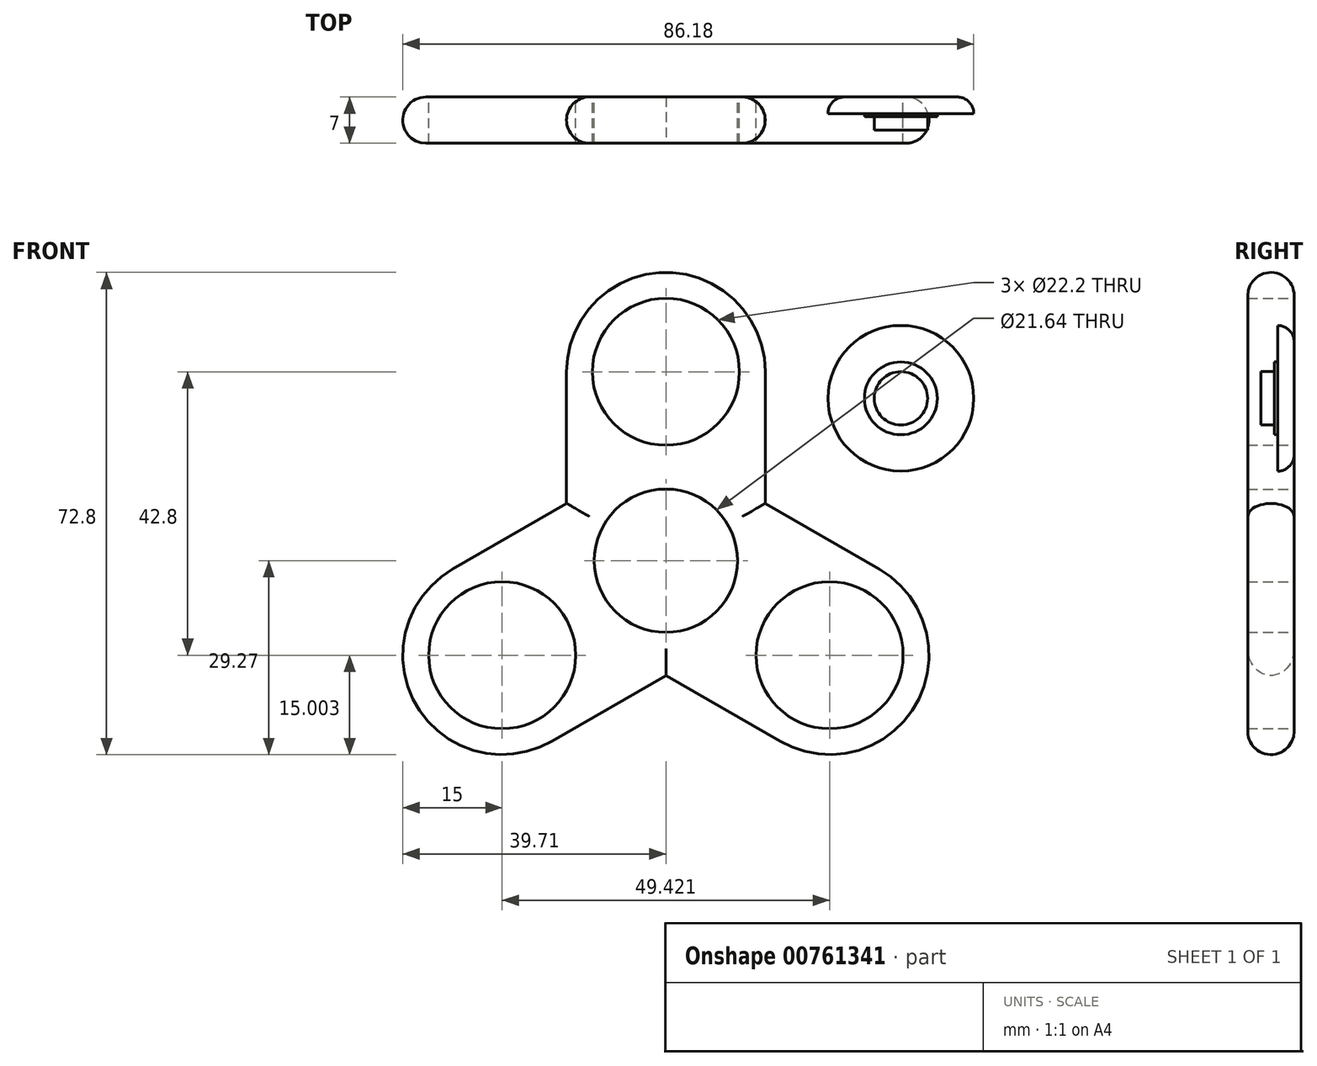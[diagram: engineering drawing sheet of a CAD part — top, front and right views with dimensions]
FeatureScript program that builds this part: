
annotation { "Feature Type Name" : "Feature", "Feature Type Description" : "" }
export const myFeature = defineFeature(function(context is Context, id is Id, definition is map)
    precondition{}
    {
        {
            var Q0;
            Q0=qCreatedBy(makeId("Front.planeOp"),FACE);
            var sketch = newSketch(context, id + "F0", { "sketchPlane" : qUnion([Q0])});
            skCircle(sketch, "E0", {"center": v(35.47, 24.52) * mm, "radius": 11 * mm});
            skCircle(sketch, "E1", {"center": v(35.47, 24.52) * mm, "radius": 5.5 * mm});
            skCircle(sketch, "E2", {"center": v(35.47, 24.52) * mm, "radius": 4.03 * mm});
            skSolve(sketch);
        }
        {
            var Q0;
            Q0=makeQuery(id+"F0.imprint","IMPRINT",FACE,{"disambiguationData":[TD([[makeQuery(id+"F0.imprint","IMPRINT",EDGE,{"derivedFrom":sQuery(id+"F0.wireOp",EDGE,"E0")}),1.0]])]});
            extrude(context, id + "F1", {"entities" : qUnion([Q0]), "depth" : 2.5 * mm, "offsetDistance" : 25 * mm});
        }
        {
            var Q0;
            Q0=makeQuery(id+"F0.imprint","IMPRINT",FACE,{"disambiguationData":[TD([[makeQuery(id+"F0.imprint","IMPRINT",EDGE,{"derivedFrom":sQuery(id+"F0.wireOp",EDGE,"E1")}),1.0]])]});
            extrude(context, id + "F2", {"entities" : qUnion([Q0]), "operationType" : NewBodyOperationType.ADD, "depth" : 3 * mm, "offsetDistance" : 25 * mm});
        }
        {
            var Q0;
            Q0=makeQuery(id+"F0.imprint","IMPRINT",FACE,{"disambiguationData":[TD([[makeQuery(id+"F0.imprint","IMPRINT",EDGE,{"derivedFrom":sQuery(id+"F0.wireOp",EDGE,"E2")}),1.0]])]});
            extrude(context, id + "F3", {"entities" : qUnion([Q0]), "operationType" : NewBodyOperationType.ADD, "depth" : 5 * mm, "offsetDistance" : 25 * mm});
        }
        {
            var Q0;
            Q0=makeQuery(id+"F1.opExtrude","CAP_EDGE",EDGE,{"disambiguationData":[OSD([sQuery(id+"F0.wireOp",EDGE,"E0")])],"isStart":true});
            fillet(context, id + "F4", {"entities" : qUnion([Q0]), "radius" : 2.5 * mm, "tangentPropagation" : true, "allowEdgeOverflow" : false});
        }
        {
            var Q0;
            Q0=qCreatedBy(makeId("Front.planeOp"),FACE);
            var sketch = newSketch(context, id + "F5", { "sketchPlane" : qUnion([Q0])});
            skCircle(sketch, "E3", {"center": v(0, 0) * mm, "radius": 10.82 * mm});
            skCircle(sketch, "E4", {"center": v(0, 28.53) * mm, "radius": 11.1 * mm});
            skCircle(sketch, "E5.1.0", {"center": v(-24.71, -14.27) * mm, "radius": 11.1 * mm});
            skCircle(sketch, "E5.2.0", {"center": v(24.71, -14.27) * mm, "radius": 11.1 * mm});
            skArc(sketch, "E6", {"start": v(15, 28.53) * mm, "mid": v(0, 43.53) * mm, "end": v(-15, 28.53) * mm});
            skLineSegment(sketch, "E7", {"start": v(-15, 28.53) * mm, "end": v(-15, 8.66) * mm});
            skLineSegment(sketch, "E8", {"start": v(15, 28.53) * mm, "end": v(15, 8.66) * mm});
            skLineSegment(sketch, "E9.1.0", {"start": v(-17.21, -27.26) * mm, "end": v(0, -17.32) * mm});
            skArc(sketch, "E9.1.1", {"start": v(-32.21, -1.28) * mm, "mid": v(-37.7, -21.77) * mm, "end": v(-17.21, -27.26) * mm});
            skLineSegment(sketch, "E9.1.2", {"start": v(-32.21, -1.28) * mm, "end": v(-15, 8.66) * mm});
            skLineSegment(sketch, "E9.2.0", {"start": v(32.21, -1.28) * mm, "end": v(15, 8.66) * mm});
            skArc(sketch, "E9.2.1", {"start": v(17.21, -27.26) * mm, "mid": v(37.7, -21.77) * mm, "end": v(32.21, -1.28) * mm});
            skLineSegment(sketch, "E9.2.2", {"start": v(17.21, -27.26) * mm, "end": v(0, -17.32) * mm});
            skPoint(sketch, "E10.orphan", {"position": v(-15, 6.28) * mm});
            skPoint(sketch, "E11.orphan", {"position": v(-13.67, 9.43) * mm});
            skPoint(sketch, "E12.orphan", {"position": v(12.94, 9.85) * mm});
            skPoint(sketch, "E13.orphan", {"position": v(15, 7.13) * mm});
            skPoint(sketch, "E14.orphan", {"position": v(2.06, -16.13) * mm});
            skPoint(sketch, "E15.orphan", {"position": v(-1.33, -16.55) * mm});
            skSolve(sketch);
        }
        {
            var Q0;
            Q0=makeQuery(id+"F5.imprint","IMPRINT",FACE,{"disambiguationData":[TD([[makeQuery(id+"F5.imprint","IMPRINT",EDGE,{"derivedFrom":sQuery(id+"F5.wireOp",EDGE,"E3")}),-1.0]])]});
            extrude(context, id + "F6", {"entities" : qUnion([Q0]), "depth" : 7 * mm, "offsetDistance" : 25 * mm});
        }
        {
            var Q0;
            Q0=makeQuery(id+"F6.opExtrude","CAP_EDGE",EDGE,{"disambiguationData":[OSD([sQuery(id+"F5.wireOp",EDGE,"E9.1.2")])],"isStart":false});
            var Q1;
            Q1=makeQuery(id+"F6.opExtrude","CAP_EDGE",EDGE,{"disambiguationData":[OSD([sQuery(id+"F5.wireOp",EDGE,"E9.1.1")])],"isStart":false});
            var Q2;
            Q2=makeQuery(id+"F6.opExtrude","CAP_EDGE",EDGE,{"disambiguationData":[OSD([sQuery(id+"F5.wireOp",EDGE,"E9.1.0")])],"isStart":false});
            var Q3;
            Q3=makeQuery(id+"F6.opExtrude","CAP_EDGE",EDGE,{"disambiguationData":[OSD([sQuery(id+"F5.wireOp",EDGE,"E9.2.2")])],"isStart":false});
            var Q4;
            Q4=makeQuery(id+"F6.opExtrude","CAP_EDGE",EDGE,{"disambiguationData":[OSD([sQuery(id+"F5.wireOp",EDGE,"E9.2.1")])],"isStart":false});
            var Q5;
            Q5=makeQuery(id+"F6.opExtrude","CAP_EDGE",EDGE,{"disambiguationData":[OSD([sQuery(id+"F5.wireOp",EDGE,"E8")])],"isStart":false});
            var Q6;
            Q6=makeQuery(id+"F6.opExtrude","CAP_EDGE",EDGE,{"disambiguationData":[OSD([sQuery(id+"F5.wireOp",EDGE,"E6")])],"isStart":false});
            var Q7;
            Q7=makeQuery(id+"F6.opExtrude","CAP_EDGE",EDGE,{"disambiguationData":[OSD([sQuery(id+"F5.wireOp",EDGE,"E7")])],"isStart":false});
            var Q8;
            Q8=makeQuery(id+"F6.opExtrude","CAP_EDGE",EDGE,{"disambiguationData":[OSD([sQuery(id+"F5.wireOp",EDGE,"E9.2.0")])],"isStart":false});
            var Q9;
            Q9=makeQuery(id+"F6.opExtrude","CAP_EDGE",EDGE,{"disambiguationData":[OSD([sQuery(id+"F5.wireOp",EDGE,"E7")])],"isStart":true});
            var Q10;
            Q10=makeQuery(id+"F6.opExtrude","CAP_EDGE",EDGE,{"disambiguationData":[OSD([sQuery(id+"F5.wireOp",EDGE,"E6")])],"isStart":true});
            var Q11;
            Q11=makeQuery(id+"F6.opExtrude","CAP_EDGE",EDGE,{"disambiguationData":[OSD([sQuery(id+"F5.wireOp",EDGE,"E9.1.2")])],"isStart":true});
            var Q12;
            Q12=makeQuery(id+"F6.opExtrude","CAP_EDGE",EDGE,{"disambiguationData":[OSD([sQuery(id+"F5.wireOp",EDGE,"E9.1.1")])],"isStart":true});
            var Q13;
            Q13=makeQuery(id+"F6.opExtrude","CAP_EDGE",EDGE,{"disambiguationData":[OSD([sQuery(id+"F5.wireOp",EDGE,"E9.2.0")])],"isStart":true});
            fillet(context, id + "F7", {"entities" : qUnion([Q0, Q1, Q2, Q3, Q4, Q5, Q6, Q7, Q8, Q9, Q10, Q11, Q12, Q13]), "radius" : 3.5 * mm, "tangentPropagation" : true, "allowEdgeOverflow" : false});
        }
    });
